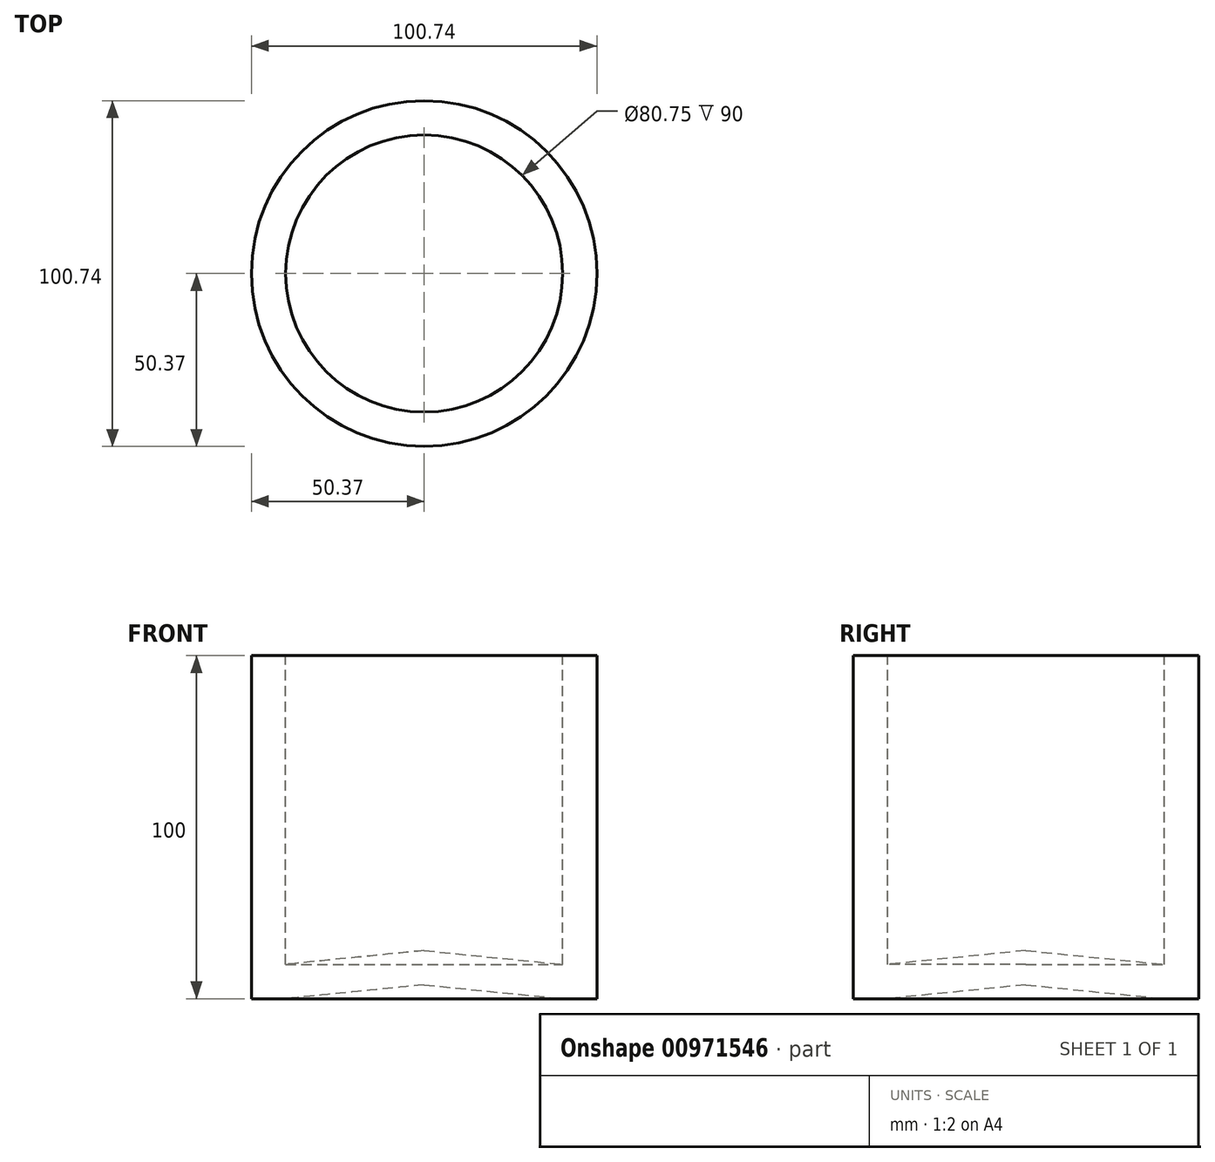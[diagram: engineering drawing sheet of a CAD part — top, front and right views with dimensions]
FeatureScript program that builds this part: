
annotation { "Feature Type Name" : "Feature", "Feature Type Description" : "" }
export const myFeature = defineFeature(function(context is Context, id is Id, definition is map)
    precondition{}
    {
        {
            var Q0;
            Q0=qCreatedBy(makeId("Front.planeOp"),FACE);
            var sketch = newSketch(context, id + "F0", { "sketchPlane" : qUnion([Q0])});
            skLineSegment(sketch, "E0", {"start": v(-50.37, 54.52) * mm, "end": v(-40.37, 54.52) * mm});
            skLineSegment(sketch, "E1", {"start": v(-40.37, 54.52) * mm, "end": v(-40.37, -35.48) * mm});
            skLineSegment(sketch, "E2", {"start": v(-40.37, -35.48) * mm, "end": v(0, -31.45) * mm});
            skLineSegment(sketch, "E3", {"start": v(0, -31.45) * mm, "end": v(0, -41.45) * mm});
            skLineSegment(sketch, "E4", {"start": v(0, -41.45) * mm, "end": v(-40.37, -45.48) * mm});
            skLineSegment(sketch, "E5", {"start": v(-40.37, -45.48) * mm, "end": v(-50.37, -45.48) * mm});
            skLineSegment(sketch, "E6", {"start": v(-50.37, -45.48) * mm, "end": v(-50.37, 54.52) * mm});
            skSolve(sketch);
        }
        {
            var Q0;
            Q0=makeQuery(id+"F0.imprint","IMPRINT",FACE,{"disambiguationData":[TD([[makeQuery(id+"F0.imprint","IMPRINT",EDGE,{"derivedFrom":sQuery(id+"F0.wireOp",EDGE,"E0")}),-1.0]])]});
            var Q1;
            Q1=sQuery(id+"F0.wireOp",EDGE,"E3");
            revolve(context, id + "F1", {"surfaceOperationType" : NewSurfaceOperationType.NEW, "entities" : qUnion([Q0]), "axis" : qUnion([Q1]), "revolveType" : RevolveType.FULL});
        }
    });
